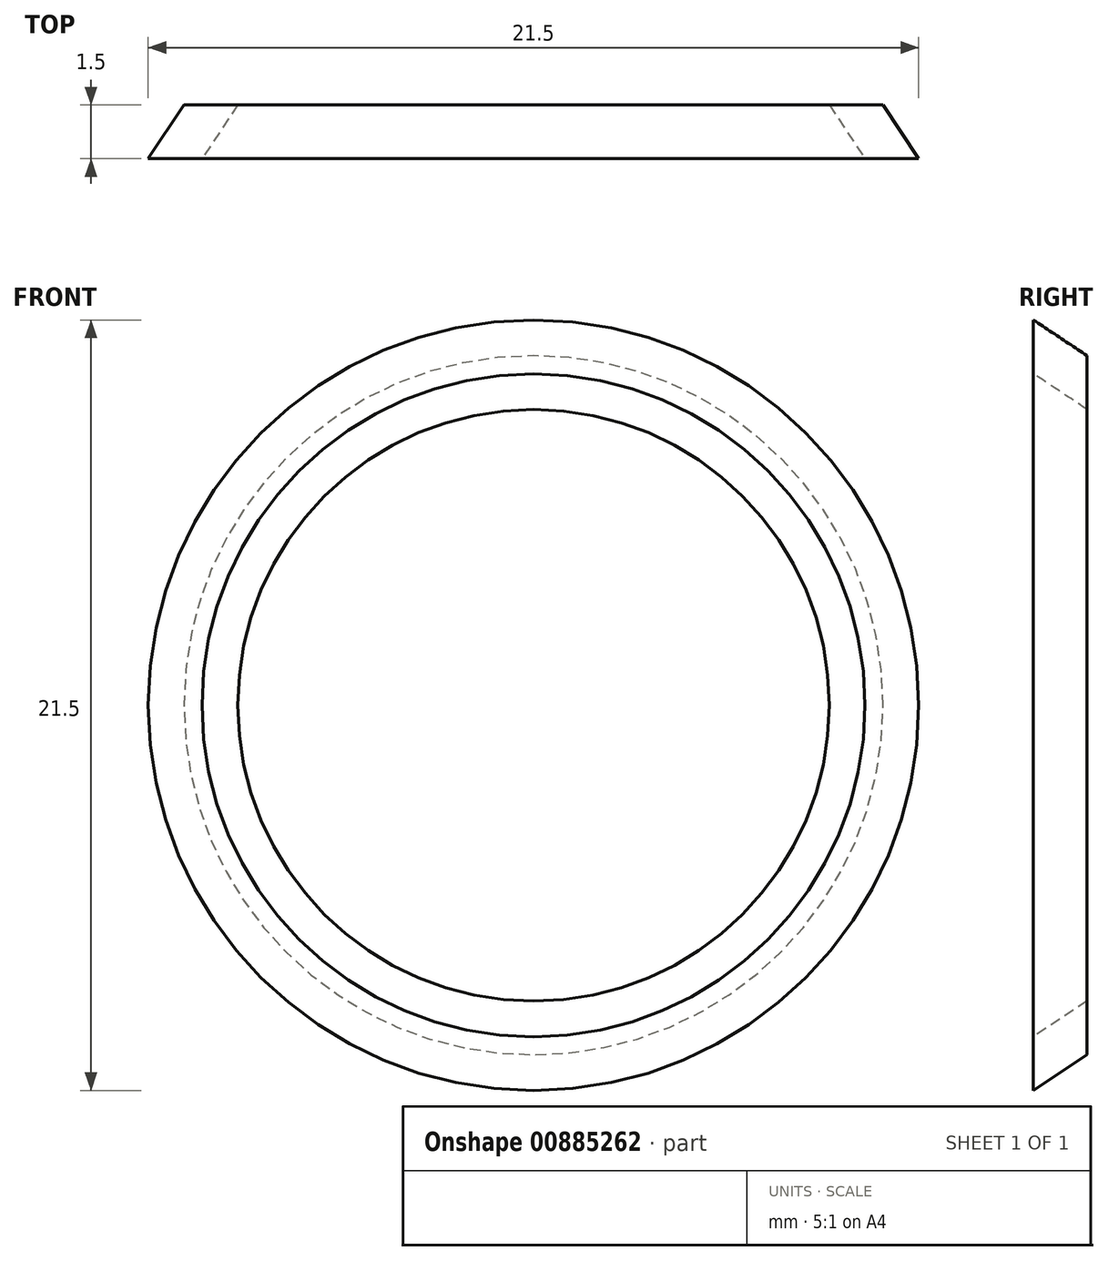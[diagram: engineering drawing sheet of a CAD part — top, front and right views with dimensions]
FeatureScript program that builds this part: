
annotation { "Feature Type Name" : "Feature", "Feature Type Description" : "" }
export const myFeature = defineFeature(function(context is Context, id is Id, definition is map)
    precondition{}
    {
        {
            var Q0;
            Q0=qCreatedBy(makeId("Top.planeOp"),FACE);
            var sketch = newSketch(context, id + "F0", { "sketchPlane" : qUnion([Q0])});
            skPoint(sketch, "E0", {"position": v(0, 0) * mm});
            skPoint(sketch, "E1", {"position": v(0, 1.5) * mm});
            skPoint(sketch, "E2", {"position": v(-8.25, 1.5) * mm});
            skLineSegment(sketch, "E3", {"start": v(-8.25, 1.5) * mm, "end": v(-9.75, 1.5) * mm});
            skPoint(sketch, "E4", {"position": v(-9.25, 0) * mm});
            skLineSegment(sketch, "E5", {"start": v(-9.25, 0) * mm, "end": v(-10.75, 0) * mm});
            skLineSegment(sketch, "E6", {"start": v(-9.75, 1.5) * mm, "end": v(-10.75, 0) * mm});
            skLineSegment(sketch, "E7", {"start": v(-8.25, 1.5) * mm, "end": v(-9.25, 0) * mm});
            skLineSegment(sketch, "E8", {"start": v(0, 66.6) * mm, "end": v(0, -32.8) * mm});
            skLineSegment(sketch, "E9", {"start": v(-8.25, 1.5) * mm, "end": v(-8.25, 0) * mm});
            skLineSegment(sketch, "E10", {"start": v(-8.25, 0) * mm, "end": v(-9.25, 0) * mm});
            skSolve(sketch);
        }
        {
            var Q0;
            Q0=makeQuery(id+"F0.imprint","IMPRINT",FACE,{"disambiguationData":[TD([[makeQuery(id+"F0.imprint","IMPRINT",EDGE,{"derivedFrom":sQuery(id+"F0.wireOp",EDGE,"E3")}),1.0]])]});
            var Q1;
            Q1=sQuery(id+"F0.wireOp",EDGE,"E8");
            revolve(context, id + "F1", {"surfaceOperationType" : NewSurfaceOperationType.NEW, "entities" : qUnion([Q0]), "axis" : qUnion([Q1]), "revolveType" : RevolveType.FULL});
        }
    });
